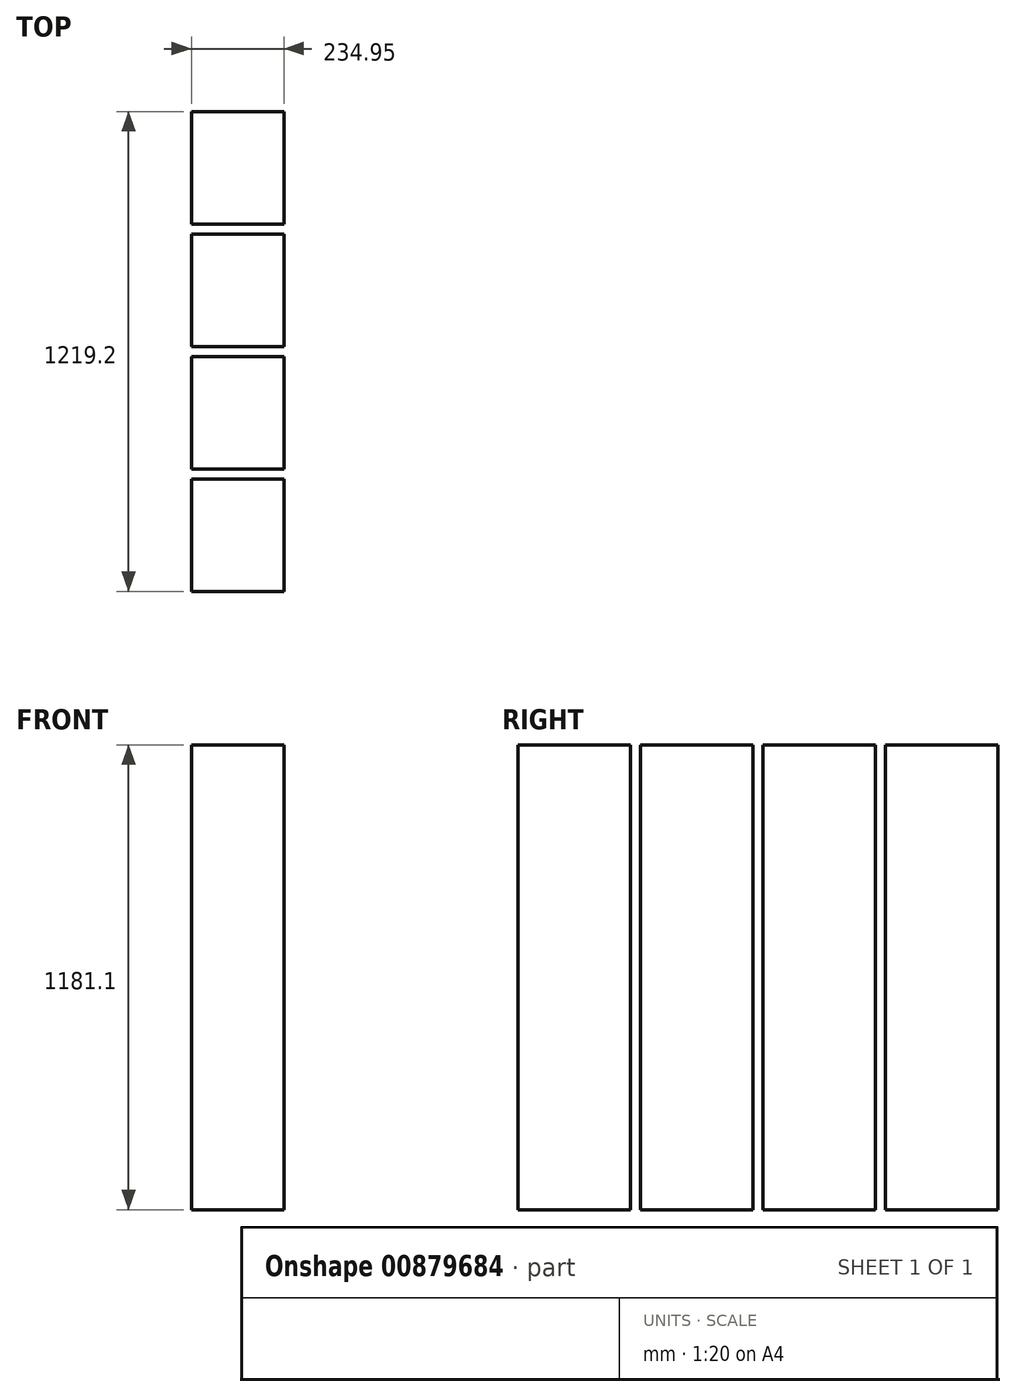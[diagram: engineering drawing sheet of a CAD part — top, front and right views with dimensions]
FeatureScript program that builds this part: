
annotation { "Feature Type Name" : "Feature", "Feature Type Description" : "" }
export const myFeature = defineFeature(function(context is Context, id is Id, definition is map)
    precondition{}
    {
        {
            var Q0;
            Q0=qCreatedBy(makeId("Top.planeOp"),FACE);
            var sketch = newSketch(context, id + "F0", { "sketchPlane" : qUnion([Q0])});
            skLineSegment(sketch, "E0.bottom", {"start": v(-380.95, 627.09) * mm, "end": v(-146, 627.09) * mm});
            skLineSegment(sketch, "E0.top", {"start": v(-380.95, 341.34) * mm, "end": v(-146, 341.34) * mm});
            skLineSegment(sketch, "E0.left", {"start": v(-380.95, 627.09) * mm, "end": v(-380.95, 341.34) * mm});
            skLineSegment(sketch, "E0.right", {"start": v(-146, 627.09) * mm, "end": v(-146, 341.34) * mm});
            skLineSegment(sketch, "E1.bottom", {"start": v(-380.95, 315.94) * mm, "end": v(-146, 315.94) * mm});
            skLineSegment(sketch, "E1.top", {"start": v(-380.95, 30.19) * mm, "end": v(-146, 30.19) * mm});
            skLineSegment(sketch, "E1.left", {"start": v(-380.95, 315.94) * mm, "end": v(-380.95, 30.19) * mm});
            skLineSegment(sketch, "E1.right", {"start": v(-146, 315.94) * mm, "end": v(-146, 30.19) * mm});
            skLineSegment(sketch, "E2.bottom", {"start": v(-380.95, 4.79) * mm, "end": v(-146, 4.79) * mm});
            skLineSegment(sketch, "E2.top", {"start": v(-380.95, -280.96) * mm, "end": v(-146, -280.96) * mm});
            skLineSegment(sketch, "E2.left", {"start": v(-380.95, 4.79) * mm, "end": v(-380.95, -280.96) * mm});
            skLineSegment(sketch, "E2.right", {"start": v(-146, 4.79) * mm, "end": v(-146, -280.96) * mm});
            skLineSegment(sketch, "E3.bottom", {"start": v(-380.95, -306.36) * mm, "end": v(-146, -306.36) * mm});
            skLineSegment(sketch, "E3.top", {"start": v(-380.95, -592.11) * mm, "end": v(-146, -592.11) * mm});
            skLineSegment(sketch, "E3.left", {"start": v(-380.95, -306.36) * mm, "end": v(-380.95, -592.11) * mm});
            skLineSegment(sketch, "E3.right", {"start": v(-146, -306.36) * mm, "end": v(-146, -592.11) * mm});
            skSolve(sketch);
        }
        {
            var Q0;
            Q0=makeQuery(id+"F0.imprint","IMPRINT",FACE,{"disambiguationData":[TD([[makeQuery(id+"F0.imprint","IMPRINT",EDGE,{"derivedFrom":sQuery(id+"F0.wireOp",EDGE,"E0.bottom")}),-1.0]])]});
            var Q1;
            Q1=makeQuery(id+"F0.imprint","IMPRINT",FACE,{"disambiguationData":[TD([[makeQuery(id+"F0.imprint","IMPRINT",EDGE,{"derivedFrom":sQuery(id+"F0.wireOp",EDGE,"E1.bottom")}),-1.0]])]});
            var Q2;
            Q2=makeQuery(id+"F0.imprint","IMPRINT",FACE,{"disambiguationData":[TD([[makeQuery(id+"F0.imprint","IMPRINT",EDGE,{"derivedFrom":sQuery(id+"F0.wireOp",EDGE,"E2.bottom")}),-1.0]])]});
            var Q3;
            Q3=makeQuery(id+"F0.imprint","IMPRINT",FACE,{"disambiguationData":[TD([[makeQuery(id+"F0.imprint","IMPRINT",EDGE,{"derivedFrom":sQuery(id+"F0.wireOp",EDGE,"E3.bottom")}),-1.0]])]});
            extrude(context, id + "F1", {"entities" : qUnion([Q0, Q1, Q2, Q3]), "depth" : 1181.1 * mm, "offsetDistance" : 25.4 * mm});
        }
    });
